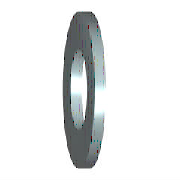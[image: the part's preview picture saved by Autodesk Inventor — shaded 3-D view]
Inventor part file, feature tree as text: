
AUTODESK INVENTOR PART (.ipt)
format: ipt  version: 2013 (Build 170138000, 138)  size: 106,496 bytes
history: native  units: mm (DEFAULTED — no unit token found)
features: other x1, plane x1, sketch x1
ambient origin geometry x7: Origin, YZ Plane, XY Plane, X Axis, Y Axis, Z Axis, Center Point
bodies: Solid1 (feature_tree), Body (feature_tree)
feature tree (3):
  other  "Work Axis1"
  plane  "Work Plane1"
  sketch  "Sketch"  dims[d0=14.2748mm d1=34.925mm d2=2.7686mm d3=0.0mm d4=0.0mm d5=0.0mm d6=0.0mm d7=0.0mm]
